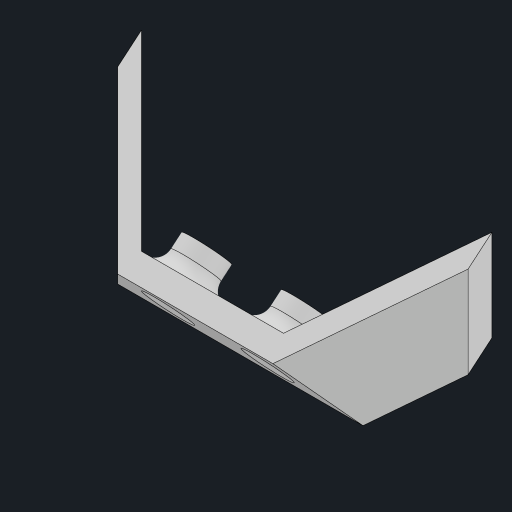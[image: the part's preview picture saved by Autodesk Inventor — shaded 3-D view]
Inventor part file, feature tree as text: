
AUTODESK INVENTOR PART (.ipt)
format: ipt  version: 2023 (Build 270158000, 158)  size: 184,320 bytes
history: native  units: mm
features: sketch x7, extrude x5, other x3, hole x1, fillet x1, chamfer x1, projected_geometry x1
ambient origin geometry x8: Origin, YZ Plane, XZ Plane, XY Plane, X Axis, Y Axis, Z Axis, Center Point
bodies: Body1 (feature_tree)
feature tree (19):
  other  "ソリッド1"
  extrude  "押し出し1"  Depth=40.0mm
  extrude  "押し出し2"  Depth=2.4mm
  other  "作業平面1"
  sketch  "スケッチ4"
  other  "作業平面2"
  extrude  "押し出し3"  Depth=50.0mm TaperAngle=0.0deg
  extrude  "押し出し4"  Depth=6.981317mm
  hole  "穴1"  [1 undecoded]
  extrude  "押し出し5"  Depth=50.0mm TaperAngle=0.0deg
  fillet  "フィレット1"  [1 undecoded]
  chamfer  "面取り1"  Distance=14.2mm
  sketch  "スケッチ1"
  sketch  "スケッチ2"
  sketch  "スケッチ5"
  sketch  "スケッチ6"
  sketch  "スケッチ7"
  projected_geometry  "投影ループ1"
  sketch  "スケッチ9"
note: 2 required parameter values undecoded (feature->parameter linkage not recoverable at this tier; creation-order binding heuristic only, values carry confidence <= 0.55)
